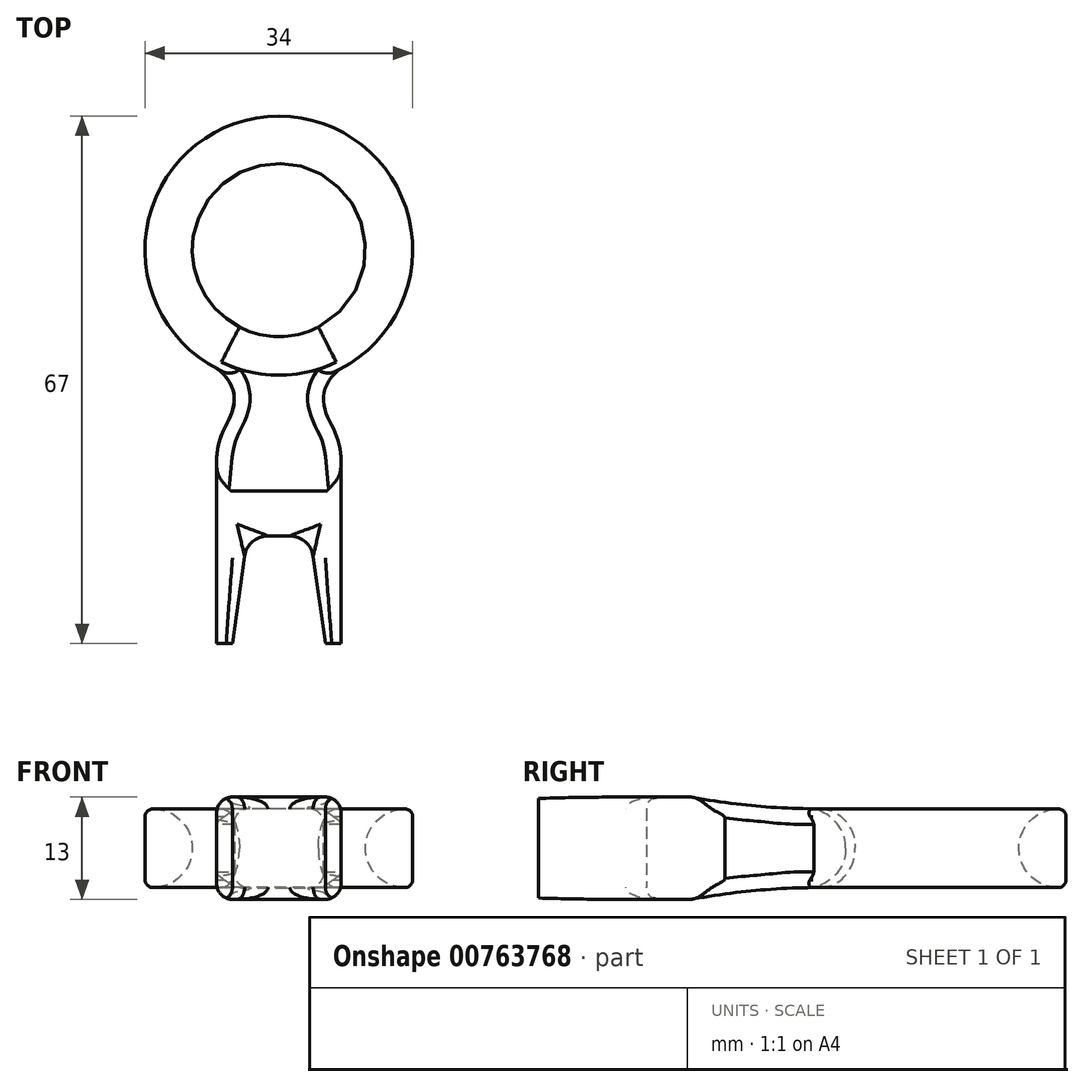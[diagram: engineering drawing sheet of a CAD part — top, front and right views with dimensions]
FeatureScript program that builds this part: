
annotation { "Feature Type Name" : "Feature", "Feature Type Description" : "" }
export const myFeature = defineFeature(function(context is Context, id is Id, definition is map)
    precondition{}
    {
        {
            var Q0;
            Q0=qCreatedBy(makeId("Top.planeOp"),FACE);
            var sketch = newSketch(context, id + "F0", { "sketchPlane" : qUnion([Q0])});
            skLineSegment(sketch, "E0.top", {"start": v(-7.9, 23.68) * mm, "end": v(7.9, 23.68) * mm, "construction": true});
            skLineSegment(sketch, "E0.left", {"start": v(-7.9, 0) * mm, "end": v(-7.9, 23.68) * mm});
            skLineSegment(sketch, "E0.right", {"start": v(7.9, 0) * mm, "end": v(7.9, 23.68) * mm});
            skLineSegment(sketch, "E1", {"start": v(-7.9, 0) * mm, "end": v(-5.9, 0) * mm});
            skLineSegment(sketch, "E2", {"start": v(7.9, 0) * mm, "end": v(5.9, 0) * mm});
            skLineSegment(sketch, "E3", {"start": v(-18.15, 13.68) * mm, "end": v(26.15, 13.68) * mm, "construction": true});
            skFitSpline(sketch, "E4", {"points": [v(-7.9, 23.68) * mm, v(-6.1, 29.01) * mm, v(-7.9, 34.95) * mm], "startDerivative": vector(1.77, 18.06) * mm, "endDerivative": vector(-16.24, 12.38) * mm});
            skFitSpline(sketch, "E5.MirrorCS", {"points": [v(7.9, 23.68) * mm, v(6.1, 29.01) * mm, v(7.9, 34.95) * mm], "startDerivative": vector(-1.77, 18.06) * mm, "endDerivative": vector(16.24, 12.38) * mm});
            skArc(sketch, "E6", {"start": v(7.9, 34.95) * mm, "mid": v(0, 67) * mm, "end": v(-7.9, 34.95) * mm});
            skCircle(sketch, "E7", {"center": v(0, 50) * mm, "radius": 11 * mm});
            skLineSegment(sketch, "E8", {"start": v(-5.9, 0) * mm, "end": v(-4, 13.68) * mm});
            skLineSegment(sketch, "E9", {"start": v(-4, 13.68) * mm, "end": v(4, 13.68) * mm});
            skLineSegment(sketch, "E10", {"start": v(4, 13.68) * mm, "end": v(5.9, 0) * mm});
            skSolve(sketch);
        }
        {
            var Q0;
            Q0=makeQuery(id+"F0.imprint","IMPRINT",FACE,{"disambiguationData":[TD([[makeQuery(id+"F0.imprint","IMPRINT",EDGE,{"derivedFrom":sQuery(id+"F0.wireOp",EDGE,"E0.left")}),-1.0]])]});
            extrude(context, id + "F1", {"entities" : qUnion([Q0]), "depth" : 13 * mm, "offsetDistance" : 25 * mm});
        }
        {
            var Q0;
            Q0=qCreatedBy(makeId("Right.planeOp"),FACE);
            var sketch = newSketch(context, id + "F2", { "sketchPlane" : qUnion([Q0])});
            skLineSegment(sketch, "E11", {"start": v(68, 11.5) * mm, "end": v(35.76, 11.5) * mm});
            skLineSegment(sketch, "E12", {"start": v(19.36, 13) * mm, "end": v(68, 13) * mm});
            skLineSegment(sketch, "E13", {"start": v(68, 13) * mm, "end": v(68, 11.5) * mm});
            skLineSegment(sketch, "E14", {"start": v(80.15, 6.5) * mm, "end": v(-3.68, 6.5) * mm, "construction": true});
            skArc(sketch, "E15", {"start": v(19.36, 13) * mm, "mid": v(27.53, 11.88) * mm, "end": v(35.76, 11.5) * mm});
            skLineSegment(sketch, "E16.MirrorCS", {"start": v(68, 1.5) * mm, "end": v(35.76, 1.5) * mm});
            skArc(sketch, "E17.MirrorCS", {"start": v(19.36, 0) * mm, "mid": v(27.53, 1.12) * mm, "end": v(35.76, 1.5) * mm});
            skLineSegment(sketch, "E18.MirrorCS", {"start": v(19.36, 0) * mm, "end": v(68, 0) * mm});
            skLineSegment(sketch, "E19.MirrorCS", {"start": v(68, 0) * mm, "end": v(68, 1.5) * mm});
            skSolve(sketch);
        }
        {
            var Q0;
            Q0=qSketchRegion(id+"F2",true);
            extrude(context, id + "F3", {"entities" : qUnion([Q0]), "operationType" : NewBodyOperationType.REMOVE, "endBound" : BoundingType.SYMMETRIC, "oppositeDirection" : true, "depth" : 60 * mm, "offsetDistance" : 25 * mm});
        }
        {
            var Q0;
            Q0=makeQuery(id+"F3.boolean.opBoolean","INTERSECT",EDGE,{"derivedFrom":[makeQuery(id+"F1.opExtrude","SWEPT_FACE",FACE,{"disambiguationData":[OSD([sQuery(id+"F0.wireOp",EDGE,"E7")])]}),makeQuery(id+"F3.opExtrude","SWEPT_FACE",FACE,{"disambiguationData":[OSD([sQuery(id+"F2.wireOp",EDGE,"E11")])]})]});
            var Q1;
            Q1=makeQuery(id+"F3.boolean.opBoolean","INTERSECT",EDGE,{"derivedFrom":[makeQuery(id+"F1.opExtrude","SWEPT_FACE",FACE,{"disambiguationData":[OSD([sQuery(id+"F0.wireOp",EDGE,"E7")])]}),makeQuery(id+"F3.opExtrude","SWEPT_FACE",FACE,{"disambiguationData":[OSD([sQuery(id+"F2.wireOp",EDGE,"E16.MirrorCS")])]})]});
            fillet(context, id + "F4", {"entities" : qUnion([Q0, Q1]), "radius" : 5 * mm, "tangentPropagation" : true, "allowEdgeOverflow" : false});
        }
        {
            var Q0;
            Q0=makeQuery(id+"F3.boolean.opBoolean","INTERSECT",EDGE,{"derivedFrom":[makeQuery(id+"F1.opExtrude","SWEPT_FACE",FACE,{"disambiguationData":[OSD([sQuery(id+"F0.wireOp",EDGE,"E5.MirrorCS")])]}),makeQuery(id+"F3.opExtrude","SWEPT_FACE",FACE,{"disambiguationData":[OSD([sQuery(id+"F2.wireOp",EDGE,"E17.MirrorCS")])]})]});
            var Q1;
            Q1=makeQuery(id+"F1.opExtrude","CAP_EDGE",EDGE,{"disambiguationData":[OSD([sQuery(id+"F0.wireOp",EDGE,"E0.right")])],"isStart":true});
            var Q2;
            Q2=makeQuery(id+"F3.boolean.opBoolean","INTERSECT",EDGE,{"derivedFrom":[makeQuery(id+"F1.opExtrude","SWEPT_FACE",FACE,{"disambiguationData":[OSD([sQuery(id+"F0.wireOp",EDGE,"E4")])]}),makeQuery(id+"F3.opExtrude","SWEPT_FACE",FACE,{"disambiguationData":[OSD([sQuery(id+"F2.wireOp",EDGE,"E17.MirrorCS")])]})]});
            var Q3;
            Q3=makeQuery(id+"F1.opExtrude","CAP_EDGE",EDGE,{"disambiguationData":[OSD([sQuery(id+"F0.wireOp",EDGE,"E0.left")])],"isStart":true});
            var Q4;
            Q4=makeQuery(id+"F3.boolean.opBoolean","INTERSECT",EDGE,{"derivedFrom":[makeQuery(id+"F1.opExtrude","SWEPT_FACE",FACE,{"disambiguationData":[OSD([sQuery(id+"F0.wireOp",EDGE,"E5.MirrorCS")])]}),makeQuery(id+"F3.opExtrude","SWEPT_FACE",FACE,{"disambiguationData":[OSD([sQuery(id+"F2.wireOp",EDGE,"E15")])]})]});
            var Q5;
            Q5=makeQuery(id+"F1.opExtrude","CAP_EDGE",EDGE,{"disambiguationData":[OSD([sQuery(id+"F0.wireOp",EDGE,"E0.right")])],"isStart":false});
            var Q6;
            Q6=makeQuery(id+"F3.boolean.opBoolean","INTERSECT",EDGE,{"derivedFrom":[makeQuery(id+"F1.opExtrude","SWEPT_FACE",FACE,{"disambiguationData":[OSD([sQuery(id+"F0.wireOp",EDGE,"E4")])]}),makeQuery(id+"F3.opExtrude","SWEPT_FACE",FACE,{"disambiguationData":[OSD([sQuery(id+"F2.wireOp",EDGE,"E15")])]})]});
            var Q7;
            Q7=makeQuery(id+"F1.opExtrude","CAP_EDGE",EDGE,{"disambiguationData":[OSD([sQuery(id+"F0.wireOp",EDGE,"E0.left")])],"isStart":false});
            fillet(context, id + "F5", {"entities" : qUnion([Q0, Q1, Q2, Q3, Q4, Q5, Q6, Q7]), "radius" : 2 * mm, "tangentPropagation" : true, "allowEdgeOverflow" : false});
        }
        {
            var Q0;
            Q0=makeQuery(id+"F3.boolean.opBoolean","INTERSECT",EDGE,{"derivedFrom":[makeQuery(id+"F1.opExtrude","SWEPT_FACE",FACE,{"disambiguationData":[OSD([sQuery(id+"F0.wireOp",EDGE,"E6")])]}),makeQuery(id+"F3.opExtrude","SWEPT_FACE",FACE,{"disambiguationData":[OSD([sQuery(id+"F2.wireOp",EDGE,"E11")])]})]});
            var Q1;
            Q1=makeQuery(id+"F3.boolean.opBoolean","INTERSECT",EDGE,{"derivedFrom":[makeQuery(id+"F1.opExtrude","SWEPT_FACE",FACE,{"disambiguationData":[OSD([sQuery(id+"F0.wireOp",EDGE,"E6")])]}),makeQuery(id+"F3.opExtrude","SWEPT_FACE",FACE,{"disambiguationData":[OSD([sQuery(id+"F2.wireOp",EDGE,"E16.MirrorCS")])]})]});
            fillet(context, id + "F6", {"entities" : qUnion([Q0, Q1]), "radius" : 1 * mm, "tangentPropagation" : true, "allowEdgeOverflow" : false});
        }
        {
            var Q0;
            Q0=makeQuery(id+"F1.opExtrude","CAP_EDGE",EDGE,{"disambiguationData":[OSD([sQuery(id+"F0.wireOp",EDGE,"E9")])],"isStart":true});
            var Q1;
            Q1=makeQuery(id+"F1.opExtrude","CAP_EDGE",EDGE,{"disambiguationData":[OSD([sQuery(id+"F0.wireOp",EDGE,"E8")])],"isStart":true});
            var Q2;
            Q2=makeQuery(id+"F1.opExtrude","CAP_EDGE",EDGE,{"disambiguationData":[OSD([sQuery(id+"F0.wireOp",EDGE,"E10")])],"isStart":true});
            var Q3;
            Q3=makeQuery(id+"F1.opExtrude","CAP_EDGE",EDGE,{"disambiguationData":[OSD([sQuery(id+"F0.wireOp",EDGE,"E10")])],"isStart":false});
            var Q4;
            Q4=makeQuery(id+"F1.opExtrude","CAP_EDGE",EDGE,{"disambiguationData":[OSD([sQuery(id+"F0.wireOp",EDGE,"E9")])],"isStart":false});
            var Q5;
            Q5=makeQuery(id+"F1.opExtrude","CAP_EDGE",EDGE,{"disambiguationData":[OSD([sQuery(id+"F0.wireOp",EDGE,"E8")])],"isStart":false});
            fillet(context, id + "F7", {"entities" : qUnion([Q0, Q1, Q2, Q3, Q4, Q5]), "radius" : 1.5 * mm, "tangentPropagation" : true, "allowEdgeOverflow" : false});
        }
        {
            var Q0;
            Q0=makeQuery(id+"F1.opExtrude","SWEPT_EDGE",EDGE,{"disambiguationData":[OSD([sQuery(id+"F0.wireOp",EDGE,"E8"),sQuery(id+"F0.wireOp",EDGE,"E9")])]});
            var Q1;
            Q1=makeQuery(id+"F1.opExtrude","SWEPT_EDGE",EDGE,{"disambiguationData":[OSD([sQuery(id+"F0.wireOp",EDGE,"E9"),sQuery(id+"F0.wireOp",EDGE,"E10")])]});
            fillet(context, id + "F8", {"entities" : qUnion([Q0, Q1]), "radius" : 3 * mm, "tangentPropagation" : true, "allowEdgeOverflow" : false});
        }
    });
